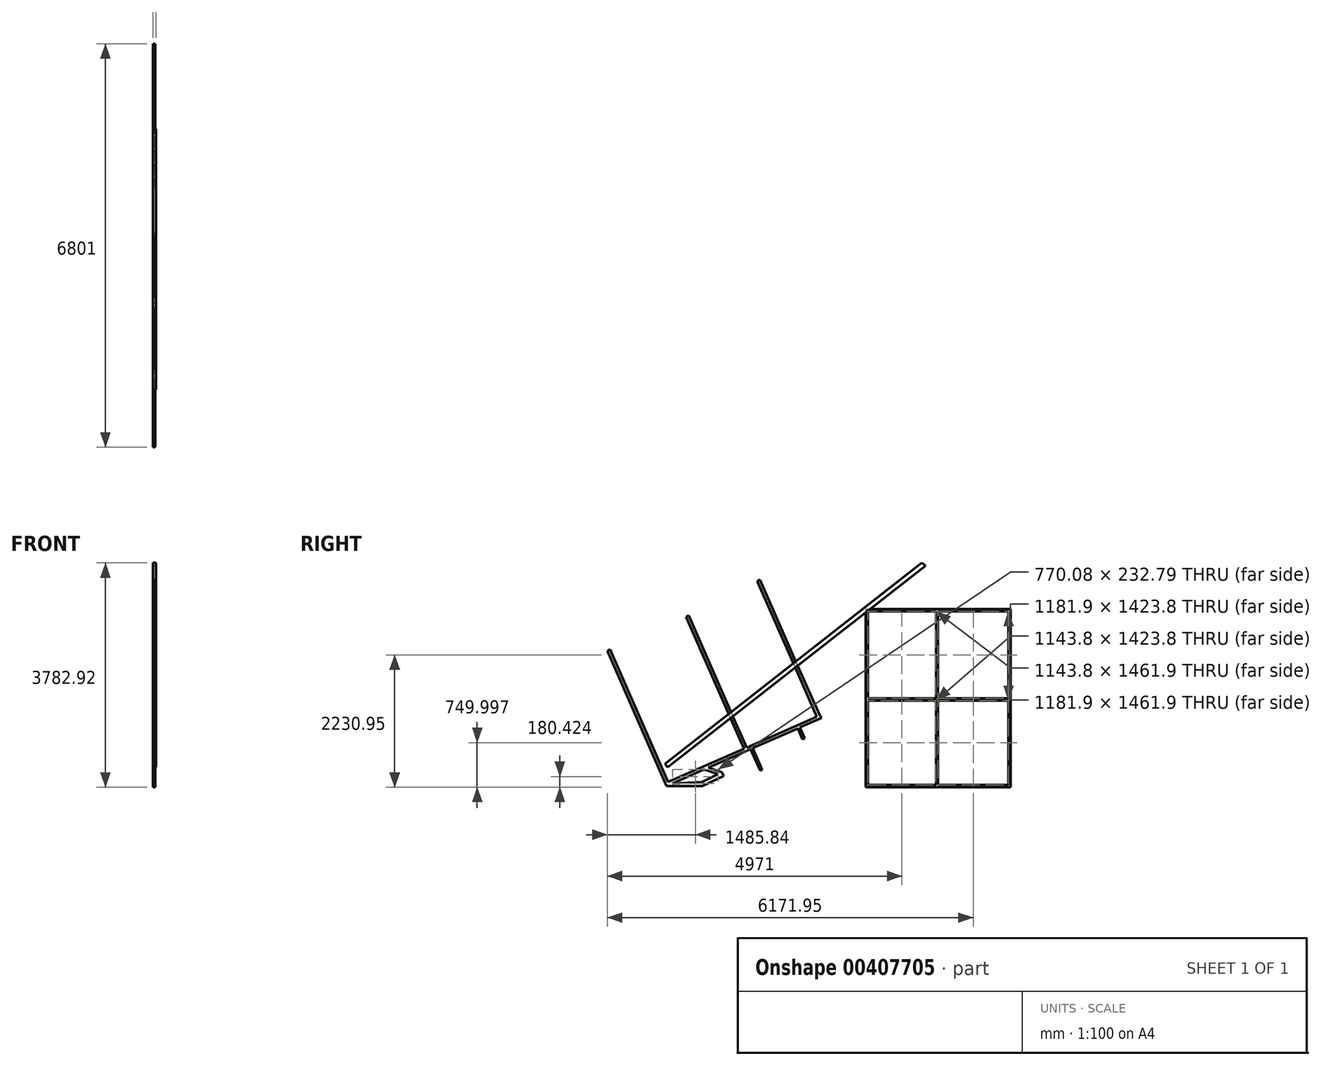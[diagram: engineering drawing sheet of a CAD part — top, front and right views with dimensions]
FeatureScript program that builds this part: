
annotation { "Feature Type Name" : "Feature", "Feature Type Description" : "" }
export const myFeature = defineFeature(function(context is Context, id is Id, definition is map)
    precondition{}
    {
        {
            var Q0;
            Q0=qCreatedBy(makeId("Right.planeOp"),FACE);
            var sketch = newSketch(context, id + "F0", { "sketchPlane" : qUnion([Q0])});
            skLineSegment(sketch, "E0.bottom", {"start": v(3433.36, 2465.07) * mm, "end": v(5873.36, 2465.07) * mm});
            skLineSegment(sketch, "E0.top", {"start": v(3433.36, -534.93) * mm, "end": v(5873.36, -534.93) * mm});
            skLineSegment(sketch, "E0.left", {"start": v(3433.36, 2465.07) * mm, "end": v(3433.36, -534.93) * mm});
            skLineSegment(sketch, "E0.right", {"start": v(5873.36, 2465.07) * mm, "end": v(5873.36, -534.93) * mm});
            skLineSegment(sketch, "E1.bottom", {"start": v(3471.46, 2426.97) * mm, "end": v(5835.26, 2426.97) * mm});
            skLineSegment(sketch, "E1.top", {"start": v(3471.46, -496.83) * mm, "end": v(5835.26, -496.83) * mm});
            skLineSegment(sketch, "E1.left", {"start": v(3471.46, 2426.97) * mm, "end": v(3471.46, -496.83) * mm});
            skLineSegment(sketch, "E1.right", {"start": v(5835.26, 2426.97) * mm, "end": v(5835.26, -496.83) * mm});
            skSolve(sketch);
        }
        {
            var Q0;
            Q0=qSketchRegion(id+"F0",true);
            extrude(context, id + "F1", {"entities" : qUnion([Q0]), "depth" : 38.1 * mm, "offsetDistance" : 25.4 * mm});
        }
        {
            var Q0;
            Q0=makeQuery(id+"F1.opExtrude","CAP_FACE",FACE,{"disambiguationData":[OSD([sQuery(id+"F0.wireOp",EDGE,"E0.bottom"),sQuery(id+"F0.wireOp",EDGE,"E0.top"),sQuery(id+"F0.wireOp",EDGE,"E0.left"),sQuery(id+"F0.wireOp",EDGE,"E0.right"),sQuery(id+"F0.wireOp",EDGE,"E1.bottom"),sQuery(id+"F0.wireOp",EDGE,"E1.top"),sQuery(id+"F0.wireOp",EDGE,"E1.left"),sQuery(id+"F0.wireOp",EDGE,"E1.right")])],"isStart":false});
            var sketch = newSketch(context, id + "F2", { "sketchPlane" : qUnion([Q0])});
            skLineSegment(sketch, "E2.bottom", {"start": v(4615.26, 2465.07) * mm, "end": v(4653.36, 2465.07) * mm});
            skLineSegment(sketch, "E2.top", {"start": v(4615.26, -534.93) * mm, "end": v(4653.36, -534.93) * mm});
            skLineSegment(sketch, "E2.left", {"start": v(4615.26, 2465.07) * mm, "end": v(4615.26, -534.93) * mm});
            skLineSegment(sketch, "E2.right", {"start": v(4653.36, 2465.07) * mm, "end": v(4653.36, -534.93) * mm});
            skSolve(sketch);
        }
        {
            var Q0;
            Q0=qSketchRegion(id+"F2",true);
            extrude(context, id + "F3", {"entities" : qUnion([Q0]), "operationType" : NewBodyOperationType.ADD, "oppositeDirection" : true, "depth" : 38.1 * mm, "offsetDistance" : 25.4 * mm});
        }
        {
            var Q0;
            Q0=makeQuery(id+"F3.boolean.opBoolean","MERGE",FACE,{"derivedFrom":[makeQuery(id+"F1.opExtrude","CAP_FACE",FACE,{"disambiguationData":[OSD([sQuery(id+"F0.wireOp",EDGE,"E0.bottom"),sQuery(id+"F0.wireOp",EDGE,"E0.top"),sQuery(id+"F0.wireOp",EDGE,"E0.left"),sQuery(id+"F0.wireOp",EDGE,"E0.right"),sQuery(id+"F0.wireOp",EDGE,"E1.bottom"),sQuery(id+"F0.wireOp",EDGE,"E1.top"),sQuery(id+"F0.wireOp",EDGE,"E1.left"),sQuery(id+"F0.wireOp",EDGE,"E1.right")])],"isStart":false}),makeQuery(id+"F3.opExtrude","CAP_FACE",FACE,{"disambiguationData":[OSD([sQuery(id+"F2.wireOp",EDGE,"E2.bottom"),sQuery(id+"F2.wireOp",EDGE,"E2.top"),sQuery(id+"F2.wireOp",EDGE,"E2.left"),sQuery(id+"F2.wireOp",EDGE,"E2.right")])],"isStart":true})]});
            var sketch = newSketch(context, id + "F4", { "sketchPlane" : qUnion([Q0])});
            skLineSegment(sketch, "E3.bottom", {"start": v(3433.36, 926.97) * mm, "end": v(5873.36, 926.97) * mm});
            skLineSegment(sketch, "E3.top", {"start": v(3433.36, 965.07) * mm, "end": v(5873.36, 965.07) * mm});
            skLineSegment(sketch, "E3.left", {"start": v(3433.36, 926.97) * mm, "end": v(3433.36, 965.07) * mm});
            skLineSegment(sketch, "E3.right", {"start": v(5873.36, 926.97) * mm, "end": v(5873.36, 965.07) * mm});
            skSolve(sketch);
        }
        {
            var Q0;
            Q0=qSketchRegion(id+"F4",true);
            extrude(context, id + "F5", {"entities" : qUnion([Q0]), "operationType" : NewBodyOperationType.ADD, "oppositeDirection" : true, "depth" : 38.1 * mm, "offsetDistance" : 25.4 * mm});
        }
        {
            var Q0;
            Q0=qCreatedBy(makeId("Right.planeOp"),FACE);
            var sketch = newSketch(context, id + "F6", { "sketchPlane" : qUnion([Q0])});
            skLineSegment(sketch, "E4", {"start": v(2689.33, 634.36) * mm, "end": v(74.1, -514.42) * mm});
            skLineSegment(sketch, "E5", {"start": v(74.1, -514.42) * mm, "end": v(53.66, -467.9) * mm});
            skLineSegment(sketch, "E6", {"start": v(53.66, -467.9) * mm, "end": v(2653.86, 674.26) * mm});
            skLineSegment(sketch, "E7", {"start": v(2653.86, 674.26) * mm, "end": v(2689.33, 634.36) * mm});
            skLineSegment(sketch, "E8", {"start": v(53.66, -467.9) * mm, "end": v(-927.64, 1766.07) * mm});
            skLineSegment(sketch, "E9", {"start": v(-927.64, 1766.07) * mm, "end": v(-881.13, 1786.5) * mm});
            skLineSegment(sketch, "E10", {"start": v(-881.13, 1786.5) * mm, "end": v(109.15, -467.9) * mm});
            skLineSegment(sketch, "E11", {"start": v(109.15, -467.9) * mm, "end": v(74.1, -514.42) * mm});
            skLineSegment(sketch, "E12", {"start": v(1381.71, 103.18) * mm, "end": v(400.4, 2337.15) * mm});
            skPoint(sketch, "E12.startSnap0", {"position": v(1353.76, 103.18) * mm});
            skPoint(sketch, "E12.startSnap1", {"position": v(1381.71, 59.97) * mm});
            skLineSegment(sketch, "E13", {"start": v(400.4, 2337.15) * mm, "end": v(446.92, 2357.58) * mm});
            skLineSegment(sketch, "E14", {"start": v(446.92, 2357.58) * mm, "end": v(1423.7, 133.9) * mm});
            skLineSegment(sketch, "E15", {"start": v(2653.86, 674.26) * mm, "end": v(1649.67, 2960.36) * mm});
            skLineSegment(sketch, "E16", {"start": v(1649.67, 2960.36) * mm, "end": v(1603.16, 2939.93) * mm});
            skLineSegment(sketch, "E17", {"start": v(1603.16, 2939.93) * mm, "end": v(2607.35, 653.83) * mm});
            skSolve(sketch);
        }
        {
            var Q0;
            Q0 = qSketchRegion(id + "F6", true);
            extrude(context, id + "F7", {"entities" : qUnion([Q0]), "depth" : 38.1 * mm, "offsetDistance" : 25.4 * mm});
        }
        {
            var Q0;
            Q0=makeQuery(id+"F7.opExtrude","CAP_FACE",FACE,{"disambiguationData":[OSD([sQuery(id+"F6.wireOp",EDGE,"E4"),sQuery(id+"F6.wireOp",EDGE,"E5"),sQuery(id+"F6.wireOp",EDGE,"E6"),sQuery(id+"F6.wireOp",EDGE,"E7"),sQuery(id+"F6.wireOp",EDGE,"E8"),sQuery(id+"F6.wireOp",EDGE,"E9"),sQuery(id+"F6.wireOp",EDGE,"E10"),sQuery(id+"F6.wireOp",EDGE,"E12"),sQuery(id+"F6.wireOp",EDGE,"E13"),sQuery(id+"F6.wireOp",EDGE,"E14"),sQuery(id+"F6.wireOp",EDGE,"E15"),sQuery(id+"F6.wireOp",EDGE,"E16"),sQuery(id+"F6.wireOp",EDGE,"E17")])],"isStart":false});
            var sketch = newSketch(context, id + "F8", { "sketchPlane" : qUnion([Q0])});
            skLineSegment(sketch, "E18", {"start": v(74.1, -514.42) * mm, "end": v(674.1, -514.42) * mm});
            skLineSegment(sketch, "E19", {"start": v(674.1, -514.42) * mm, "end": v(674.1, -447.48) * mm});
            skLineSegment(sketch, "E20", {"start": v(674.1, -447.48) * mm, "end": v(57.36, -476.32) * mm});
            skLineSegment(sketch, "E21", {"start": v(674.1, -514.42) * mm, "end": v(1035.56, -343.12) * mm});
            skLineSegment(sketch, "E22", {"start": v(1035.56, -343.12) * mm, "end": v(1006.8, -282.43) * mm});
            skLineSegment(sketch, "E23", {"start": v(1006.8, -282.43) * mm, "end": v(674.1, -447.48) * mm});
            skLineSegment(sketch, "E24", {"start": v(1035.56, -343.12) * mm, "end": v(703.12, -238.1) * mm});
            skLineSegment(sketch, "E25", {"start": v(703.12, -238.1) * mm, "end": v(1245.19, 0) * mm});
            skLineSegment(sketch, "E26", {"start": v(1006.8, -282.43) * mm, "end": v(775.73, -206.21) * mm});
            skSolve(sketch);
        }
        {
            var Q0;
            {var subQ0=sQuery(id+"F8.wireOp",EDGE,"E22");Q0=makeQuery(id+"F8.imprint","IMPRINT",FACE,{"disambiguationData":[TD([[makeQuery(id+"F8.imprint","IMPRINT",EDGE,{"derivedFrom":subQ0}),1.0]])]});}
            var Q1;
            {var subQ4=sQuery(id+"F8.wireOp",EDGE,"X8HkKhuz-kZBg-zcCL-aepn-BqZubEwAuUVQ");Q1=makeQuery(id+"F8.imprint","IMPRINT",FACE,{"disambiguationData":[TD([[makeQuery(id+"F8.imprint","IMPRINT",EDGE,{"derivedFrom":subQ4}),1.0]])]});}
            var Q2;
            {var subQ0=sQuery(id+"F8.wireOp",EDGE,"E18");Q2=makeQuery(id+"F8.imprint","IMPRINT",FACE,{"disambiguationData":[TD([[makeQuery(id+"F8.imprint","IMPRINT",EDGE,{"derivedFrom":subQ0}),1.0]])]});}
            var Q3;
            {var subQ0=sQuery(id+"F8.wireOp",EDGE,"E19");Q3=makeQuery(id+"F8.imprint","IMPRINT",FACE,{"disambiguationData":[TD([[makeQuery(id+"F8.imprint","IMPRINT",EDGE,{"derivedFrom":subQ0}),-1.0]])]});}
            extrude(context, id + "F9", {"entities" : qUnion([Q0, Q1, Q2, Q3]), "operationType" : NewBodyOperationType.ADD, "oppositeDirection" : true, "depth" : 38.1 * mm, "offsetDistance" : 25.4 * mm});
        }
        {
            var Q0;
            Q0 = qSketchRegion(id + "F8", true);
            extrude(context, id + "F10", {"entities" : qUnion([Q0]), "operationType" : NewBodyOperationType.ADD, "oppositeDirection" : true, "depth" : 38.1 * mm, "offsetDistance" : 25.4 * mm});
        }
        {
            var Q0;
            {var subQ5=sQuery(id+"F6.wireOp",EDGE,"E4");var subQ15=sQuery(id+"F6.wireOp",EDGE,"E7");Q0=makeQuery(id+"F10.boolean.opBoolean","SPLIT",FACE,{"disambiguationData":[TD([makeQuery(id+"F7.opExtrude","SWEPT_FACE",FACE,{"disambiguationData":[OSD([subQ15])]})])],"derivedFrom":makeQuery(id+"F7.opExtrude","SWEPT_FACE",FACE,{"disambiguationData":[OSD([subQ5])]})});}
            var sketch = newSketch(context, id + "F11", { "sketchPlane" : qUnion([Q0])});
            skLineSegment(sketch, "E27.bottom", {"start": v(38.1, -1445.13) * mm, "end": v(0, -1445.13) * mm});
            skLineSegment(sketch, "E27.top", {"start": v(38.1, -1407.03) * mm, "end": v(0, -1407.03) * mm});
            skLineSegment(sketch, "E27.left", {"start": v(38.1, -1445.13) * mm, "end": v(38.1, -1407.03) * mm});
            skLineSegment(sketch, "E27.right", {"start": v(0, -1445.13) * mm, "end": v(0, -1407.03) * mm});
            skLineSegment(sketch, "E28.bottom", {"start": v(38.1, -2313.9) * mm, "end": v(0, -2313.9) * mm});
            skLineSegment(sketch, "E28.top", {"start": v(38.1, -2275.8) * mm, "end": v(0, -2275.8) * mm});
            skLineSegment(sketch, "E28.left", {"start": v(38.1, -2313.9) * mm, "end": v(38.1, -2275.8) * mm});
            skLineSegment(sketch, "E28.right", {"start": v(0, -2313.9) * mm, "end": v(0, -2275.8) * mm});
            skSolve(sketch);
        }
        {
            var Q0;
            Q0 = qSketchRegion(id + "F11", true);
            extrude(context, id + "F12", {"entities" : qUnion([Q0]), "operationType" : NewBodyOperationType.ADD, "depth" : 200 * mm, "offsetDistance" : 25.4 * mm});
        }
        {
            var Q0;
            Q0=makeQuery(id+"F12.opExtrude","CAP_FACE",FACE,{"disambiguationData":[OSD([sQuery(id+"F11.wireOp",EDGE,"E27.bottom"),sQuery(id+"F11.wireOp",EDGE,"E27.top"),sQuery(id+"F11.wireOp",EDGE,"E27.left"),sQuery(id+"F11.wireOp",EDGE,"E27.right")])],"isStart":false});
            var sketch = newSketch(context, id + "F13", { "sketchPlane" : qUnion([Q0])});
            skLineSegment(sketch, "E29.bottom", {"start": v(38.1, -1445.13) * mm, "end": v(0, -1445.13) * mm});
            skLineSegment(sketch, "E29.top", {"start": v(38.1, -1407.03) * mm, "end": v(0, -1407.03) * mm});
            skLineSegment(sketch, "E29.left", {"start": v(38.1, -1445.13) * mm, "end": v(38.1, -1407.03) * mm});
            skLineSegment(sketch, "E29.right", {"start": v(0, -1445.13) * mm, "end": v(0, -1407.03) * mm});
            skSolve(sketch);
        }
        {
            var Q0;
            Q0 = qSketchRegion(id + "F13", true);
            extrude(context, id + "F14", {"entities" : qUnion([Q0]), "operationType" : NewBodyOperationType.ADD, "depth" : 200 * mm, "offsetDistance" : 25.4 * mm});
        }
        {
            var Q0;
            Q0=qCreatedBy(makeId("Right.planeOp"),FACE);
            var sketch = newSketch(context, id + "F15", { "sketchPlane" : qUnion([Q0])});
            skLineSegment(sketch, "E30", {"start": v(4438.05, 3200.82) * mm, "end": v(90.42, -201.79) * mm});
            skLineSegment(sketch, "E31", {"start": v(90.42, -201.79) * mm, "end": v(43.46, -141.78) * mm});
            skLineSegment(sketch, "E32", {"start": v(43.46, -141.78) * mm, "end": v(4374.68, 3247.99) * mm});
            skLineSegment(sketch, "E33", {"start": v(4374.68, 3247.99) * mm, "end": v(4438.05, 3200.82) * mm});
            skSolve(sketch);
        }
        {
            var Q0;
            Q0 = qSketchRegion(id + "F15", true);
            extrude(context, id + "F16", {"entities" : qUnion([Q0]), "depth" : 50.8 * mm, "offsetDistance" : 25.4 * mm});
        }
    });
